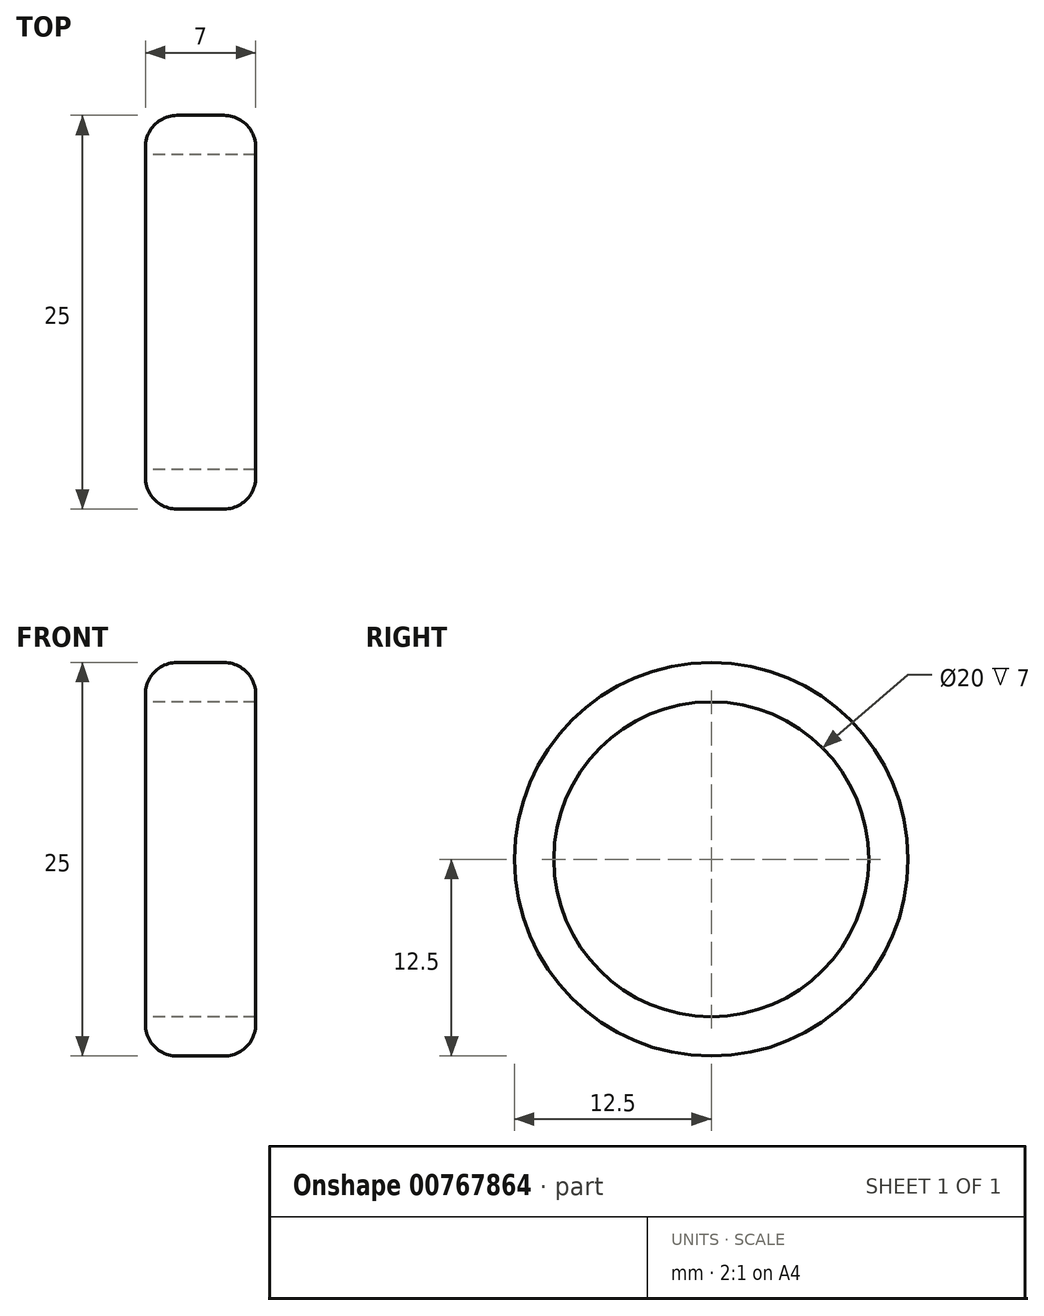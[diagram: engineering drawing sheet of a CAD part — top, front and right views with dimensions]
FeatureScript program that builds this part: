
annotation { "Feature Type Name" : "Feature", "Feature Type Description" : "" }
export const myFeature = defineFeature(function(context is Context, id is Id, definition is map)
    precondition{}
    {
        {
            var Q0;
            Q0=qCreatedBy(makeId("Right.planeOp"),FACE);
            var sketch = newSketch(context, id + "F0", { "sketchPlane" : qUnion([Q0])});
            skCircle(sketch, "E0", {"center": v(0, 0) * mm, "radius": 10 * mm});
            skCircle(sketch, "E1", {"center": v(0, 0) * mm, "radius": 12.5 * mm});
            skSolve(sketch);
        }
        {
            var Q0;
            Q0 = qSketchRegion(id + "F0", true);
            extrude(context, id + "F1", {"entities" : qUnion([Q0]), "depth" : 7 * mm, "offsetDistance" : 25 * mm});
        }
        {
            var Q0;
            Q0=makeQuery(id+"F1.opExtrude","SWEPT_FACE",FACE,{"disambiguationData":[OSD([sQuery(id+"F0.wireOp",EDGE,"E1")])]});
            var Q1;
            Q1=makeQuery(id+"F1.opExtrude","CAP_EDGE",EDGE,{"disambiguationData":[OSD([sQuery(id+"F0.wireOp",EDGE,"E1")])],"isStart":false});
            fillet(context, id + "F2", {"entities" : qUnion([Q0, Q1]), "radius" : 2 * mm, "tangentPropagation" : true, "allowEdgeOverflow" : false});
        }
    });
